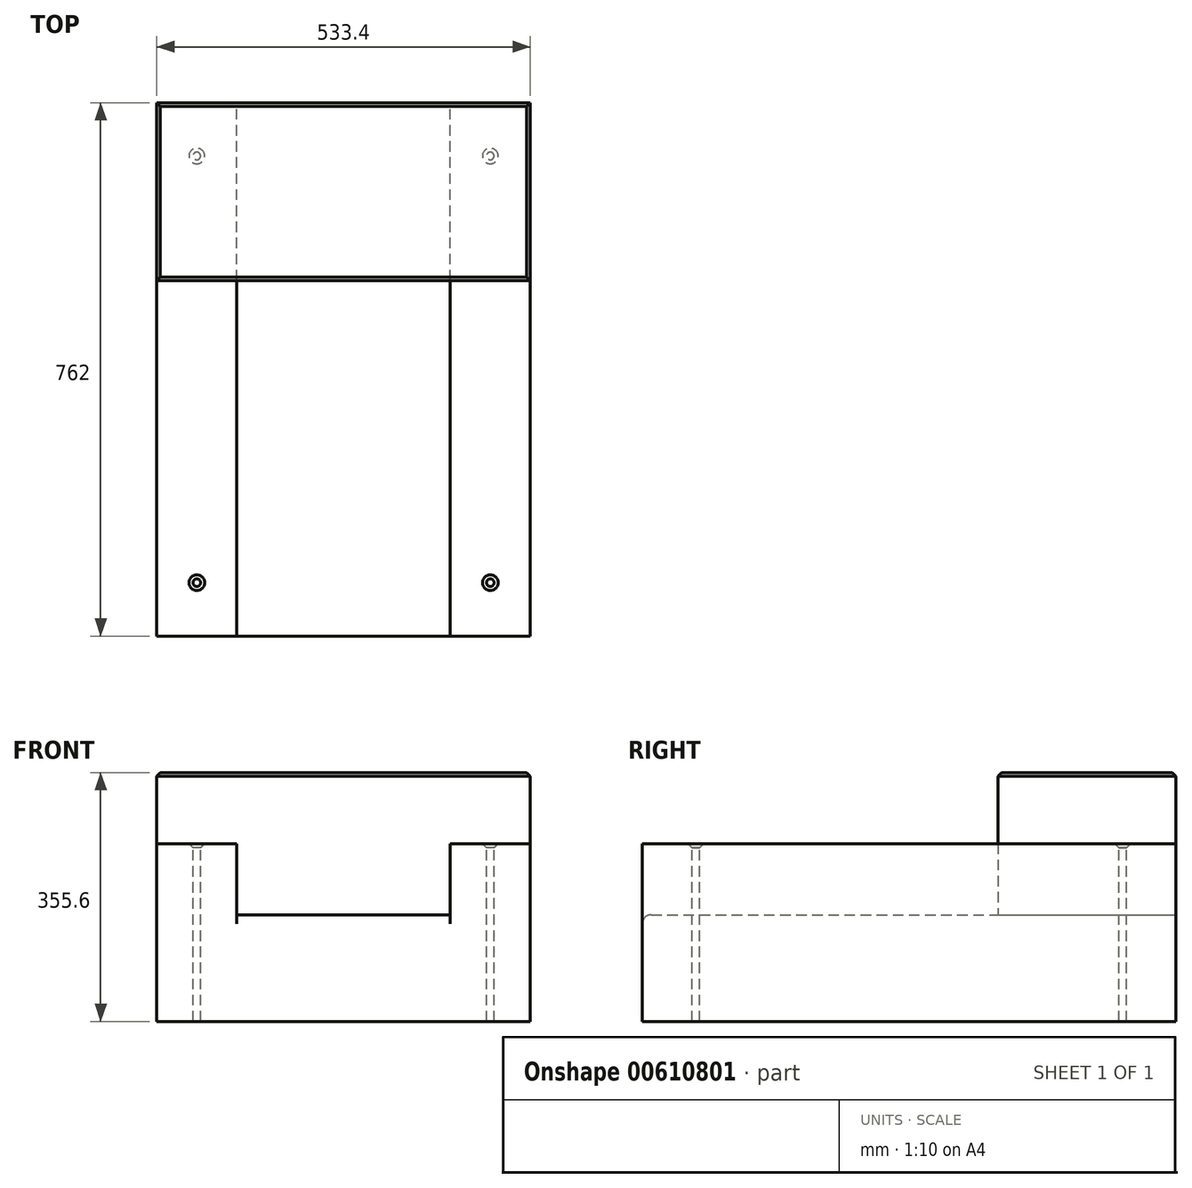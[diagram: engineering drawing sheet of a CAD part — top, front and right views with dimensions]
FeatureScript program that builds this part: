
annotation { "Feature Type Name" : "Feature", "Feature Type Description" : "" }
export const myFeature = defineFeature(function(context is Context, id is Id, definition is map)
    precondition{}
    {
        {
            var Q0;
            Q0=qCreatedBy(makeId("Front.planeOp"),FACE);
            var sketch = newSketch(context, id + "F0", { "sketchPlane" : qUnion([Q0])});
            skLineSegment(sketch, "E0.bottom", {"start": v(0, 254) * mm, "end": v(114.3, 254) * mm});
            skLineSegment(sketch, "E0.top", {"start": v(0, 0) * mm, "end": v(533.4, 0) * mm});
            skLineSegment(sketch, "E0.left", {"start": v(0, 254) * mm, "end": v(0, 0) * mm});
            skLineSegment(sketch, "E0.right", {"start": v(533.4, 254) * mm, "end": v(533.4, 0) * mm});
            skLineSegment(sketch, "E1.top", {"start": v(114.3, 152.4) * mm, "end": v(419.1, 152.4) * mm});
            skLineSegment(sketch, "E1.left", {"start": v(114.3, 254) * mm, "end": v(114.3, 152.4) * mm});
            skLineSegment(sketch, "E1.right", {"start": v(419.1, 254) * mm, "end": v(419.1, 152.4) * mm});
            skLineSegment(sketch, "E2.trimOffspring", {"start": v(419.1, 254) * mm, "end": v(533.4, 254) * mm});
            skSolve(sketch);
        }
        {
            var Q0;
            Q0=makeQuery(id+"F0.imprint","IMPRINT",FACE,{"disambiguationData":[TD([[makeQuery(id+"F0.imprint","IMPRINT",EDGE,{"derivedFrom":sQuery(id+"F0.wireOp",EDGE,"E0.bottom")}),-1.0]])]});
            extrude(context, id + "F1", {"entities" : qUnion([Q0]), "depth" : 762 * mm, "offsetDistance" : 25.4 * mm});
        }
        {
            var Q0;
            Q0=makeQuery(id+"F1.opExtrude","SWEPT_FACE",FACE,{"disambiguationData":[OSD([sQuery(id+"F0.wireOp",EDGE,"E2.trimOffspring")])]});
            var sketch = newSketch(context, id + "F2", { "sketchPlane" : qUnion([Q0])});
            skLineSegment(sketch, "E3.bottom", {"start": v(57.15, -76.2) * mm, "end": v(476.25, -76.2) * mm, "construction": true});
            skLineSegment(sketch, "E3.top", {"start": v(57.15, -685.8) * mm, "end": v(476.25, -685.8) * mm, "construction": true});
            skLineSegment(sketch, "E3.left", {"start": v(57.15, -76.2) * mm, "end": v(57.15, -685.8) * mm, "construction": true});
            skLineSegment(sketch, "E3.right", {"start": v(476.25, -76.2) * mm, "end": v(476.25, -685.8) * mm, "construction": true});
            skSolve(sketch);
        }
        {
            var Q0;
            Q0=sQuery(id+"F2.wireOp",VERTEX,"E3.left.start");
            var Q1;
            Q1=sQuery(id+"F2.wireOp",VERTEX,"E3.right.start");
            var Q2;
            Q2=sQuery(id+"F2.wireOp",VERTEX,"E3.top.end");
            var Q3;
            Q3=sQuery(id+"F2.wireOp",VERTEX,"E3.left.end");
            var Q4;
            Q4=makeQuery(id+"F1.opExtrude","SWEPT_BODY",BODY,{"disambiguationData":[OSD([sQuery(id+"F0.wireOp",EDGE,"E0.bottom"),sQuery(id+"F0.wireOp",EDGE,"E0.top"),sQuery(id+"F0.wireOp",EDGE,"E0.left"),sQuery(id+"F0.wireOp",EDGE,"E0.right"),sQuery(id+"F0.wireOp",EDGE,"E1.top"),sQuery(id+"F0.wireOp",EDGE,"E1.left"),sQuery(id+"F0.wireOp",EDGE,"E1.right"),sQuery(id+"F0.wireOp",EDGE,"E2.trimOffspring")])]});
            hole(context, id + "F3", {"style" : HoleStyle.C_SINK, "endStyle" : HoleEndStyle.THROUGH, "standardTappedOrClearance" : lookupTablePath({ "standard" : "ISO", "fit" : "Normal", "size" : "M10", "type" : "Clearance" }), "standardBlindInLast" : lookupTablePath({ "fit" : "Standard", "standard" : "ISO", "size" : "M10", "type" : "Clearance" }), "holeDiameter" : 11 * mm, "cSinkDiameter" : 22.4 * mm, "cSinkAngle" : 90 * degree, "majorDiameter" : 6.35 * mm, "isTappedThrough" : true, "tappedDepth" : 12.7 * mm, "tapClearance" : 3, "locations" : qUnion([Q0, Q1, Q2, Q3]), "scope" : qUnion([Q4])});
        }
        {
            var Q0;
            Q0=qCreatedBy(makeId("Front.planeOp"),FACE);
            var sketch = newSketch(context, id + "F4", { "sketchPlane" : qUnion([Q0])});
            skLineSegment(sketch, "E4.0", {"start": v(0, 254) * mm, "end": v(114.3, 254) * mm});
            skLineSegment(sketch, "E4.1", {"start": v(114.3, 254) * mm, "end": v(114.3, 152.4) * mm});
            skLineSegment(sketch, "E4.2", {"start": v(114.3, 152.4) * mm, "end": v(419.1, 152.4) * mm});
            skLineSegment(sketch, "E4.3", {"start": v(419.1, 254) * mm, "end": v(419.1, 152.4) * mm});
            skLineSegment(sketch, "E4.4", {"start": v(419.1, 254) * mm, "end": v(533.4, 254) * mm});
            skPoint(sketch, "E4.5", {"position": v(476.25, 254) * mm});
            skLineSegment(sketch, "E5", {"start": v(0, 254) * mm, "end": v(0, 355.6) * mm});
            skLineSegment(sketch, "E6", {"start": v(0, 355.6) * mm, "end": v(533.4, 355.6) * mm});
            skLineSegment(sketch, "E7", {"start": v(533.4, 355.6) * mm, "end": v(533.4, 254) * mm});
            skSolve(sketch);
        }
        {
            var Q0;
            Q0=makeQuery(id+"F4.imprint","IMPRINT",FACE,{"disambiguationData":[TD([[makeQuery(id+"F4.imprint","IMPRINT",EDGE,{"derivedFrom":sQuery(id+"F4.wireOp",EDGE,"E4.0")}),1.0]])]});
            extrude(context, id + "F5", {"entities" : qUnion([Q0]), "depth" : 254 * mm, "offsetDistance" : 25.4 * mm});
        }
        {
            var Q0;
            Q0=makeQuery(id+"F1.opExtrude","CAP_EDGE",EDGE,{"disambiguationData":[OSD([sQuery(id+"F0.wireOp",EDGE,"E1.top")])],"isStart":false});
            fillet(context, id + "F6", {"entities" : qUnion([Q0]), "radius" : 12.7 * mm, "tangentPropagation" : true, "allowEdgeOverflow" : false});
        }
        {
            var Q0;
            Q0=makeQuery(id+"F5.opExtrude","SWEPT_FACE",FACE,{"disambiguationData":[OSD([sQuery(id+"F4.wireOp",EDGE,"E6")])]});
            chamfer(context, id + "F7", {"entities" : qUnion([Q0]), "width" : 5.08 * mm, "tangentPropagation" : true});
        }
    });
